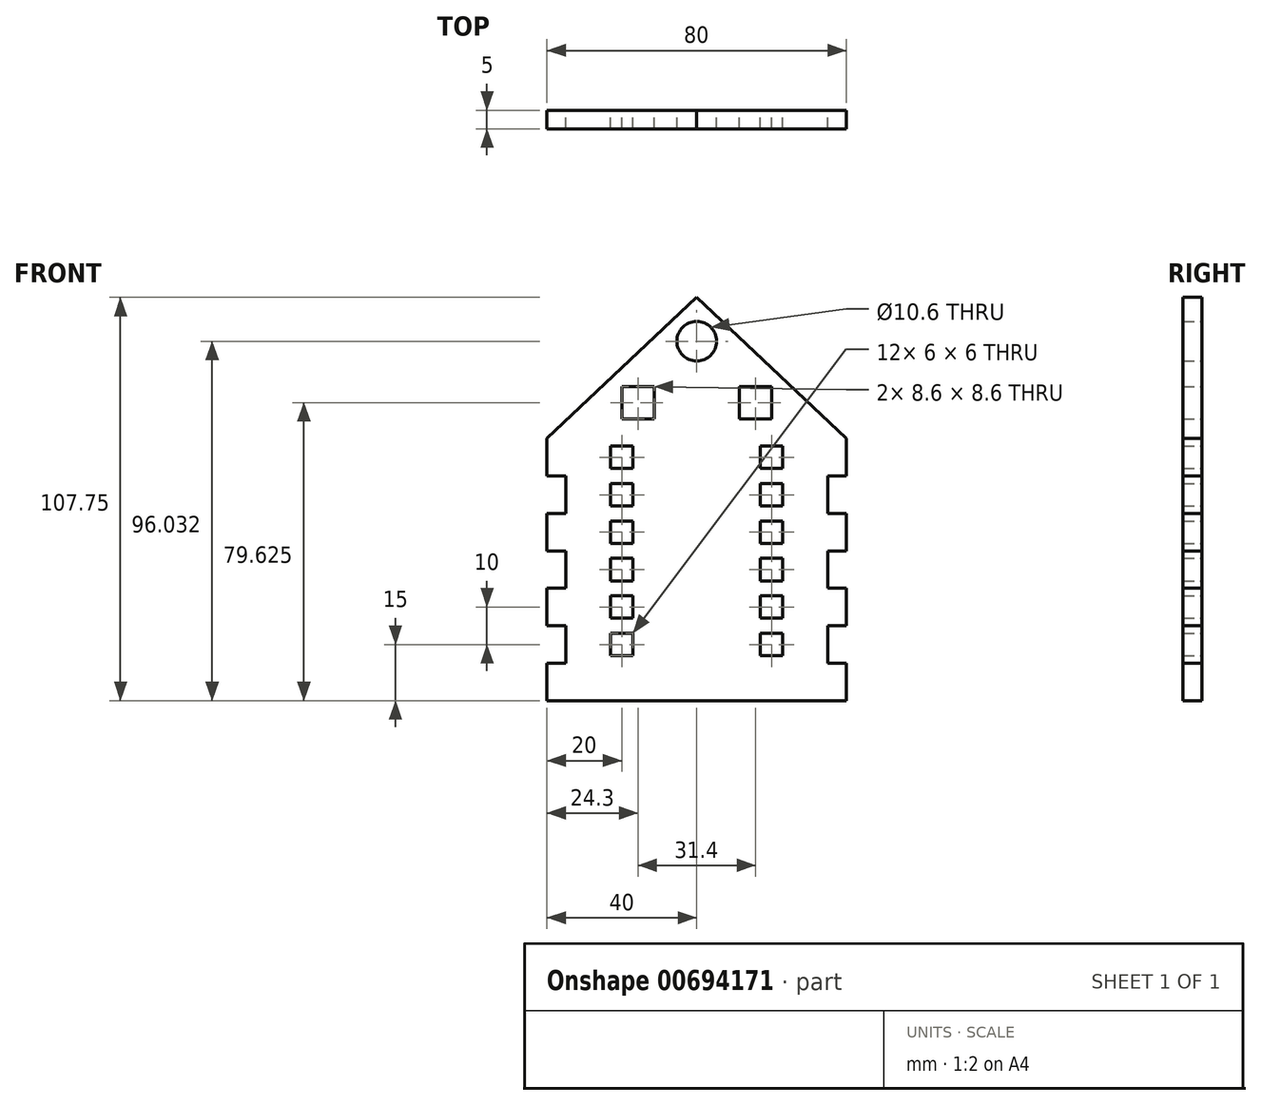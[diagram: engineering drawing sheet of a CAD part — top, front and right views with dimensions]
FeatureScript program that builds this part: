
annotation { "Feature Type Name" : "Feature", "Feature Type Description" : "" }
export const myFeature = defineFeature(function(context is Context, id is Id, definition is map)
    precondition{}
    {
        {
            var Q0;
            Q0=qCreatedBy(makeId("Front.planeOp"),FACE);
            var sketch = newSketch(context, id + "F0", { "sketchPlane" : qUnion([Q0])});
            skLineSegment(sketch, "E0.bottom", {"start": v(-40, 0) * mm, "end": v(0, 0) * mm});
            skLineSegment(sketch, "E0.top", {"start": v(-40, 70) * mm, "end": v(0, 70) * mm});
            skLineSegment(sketch, "E0.left", {"start": v(-40, 0) * mm, "end": v(-40, 10) * mm});
            skLineSegment(sketch, "E0.right", {"start": v(0, 0) * mm, "end": v(0, 70) * mm});
            skLineSegment(sketch, "E1", {"start": v(-14.13, 94.42) * mm, "end": v(-40, 70) * mm});
            skPoint(sketch, "E2.start.orphan", {"position": v(-20, 70) * mm});
            skLineSegment(sketch, "E3.bottom", {"start": v(-40, 60) * mm, "end": v(-35, 60) * mm});
            skLineSegment(sketch, "E3.top", {"start": v(-40, 50) * mm, "end": v(-35, 50) * mm});
            skLineSegment(sketch, "E3.right", {"start": v(-35, 60) * mm, "end": v(-35, 50) * mm});
            skLineSegment(sketch, "E4.bottom", {"start": v(-40, 20) * mm, "end": v(-35, 20) * mm});
            skLineSegment(sketch, "E4.top", {"start": v(-40, 10) * mm, "end": v(-35, 10) * mm});
            skLineSegment(sketch, "E4.right", {"start": v(-35, 20) * mm, "end": v(-35, 10) * mm});
            skLineSegment(sketch, "E5.bottom", {"start": v(-35, 40) * mm, "end": v(-40, 40) * mm});
            skLineSegment(sketch, "E5.top", {"start": v(-35, 30) * mm, "end": v(-40, 30) * mm});
            skLineSegment(sketch, "E5.left", {"start": v(-35, 40) * mm, "end": v(-35, 30) * mm});
            skLineSegment(sketch, "E6.trimOffspring", {"start": v(-40, 60) * mm, "end": v(-40, 70) * mm});
            skLineSegment(sketch, "E7.trimOffspring", {"start": v(-40, 40) * mm, "end": v(-40, 50) * mm});
            skLineSegment(sketch, "E8.trimOffspring", {"start": v(-40, 20) * mm, "end": v(-40, 30) * mm});
            skLineSegment(sketch, "E9.MirrorCS", {"start": v(40, 10) * mm, "end": v(35, 10) * mm});
            skLineSegment(sketch, "E10.MirrorCS", {"start": v(35, 30) * mm, "end": v(40, 30) * mm});
            skLineSegment(sketch, "E11.MirrorCS", {"start": v(35, 60) * mm, "end": v(35, 50) * mm});
            skLineSegment(sketch, "E12.MirrorCS", {"start": v(40, 60) * mm, "end": v(40, 70) * mm});
            skLineSegment(sketch, "E13.MirrorCS", {"start": v(40, 50) * mm, "end": v(35, 50) * mm});
            skLineSegment(sketch, "E14.MirrorCS", {"start": v(40, 60) * mm, "end": v(35, 60) * mm});
            skLineSegment(sketch, "E15.MirrorCS", {"start": v(40, 0) * mm, "end": v(40, 10) * mm});
            skLineSegment(sketch, "E16.MirrorCS", {"start": v(40, 40) * mm, "end": v(40, 50) * mm});
            skLineSegment(sketch, "E17.MirrorCS", {"start": v(40, 20) * mm, "end": v(35, 20) * mm});
            skLineSegment(sketch, "E18.MirrorCS", {"start": v(35, 20) * mm, "end": v(35, 10) * mm});
            skLineSegment(sketch, "E19.MirrorCS", {"start": v(40, 20) * mm, "end": v(40, 30) * mm});
            skLineSegment(sketch, "E20.MirrorCS", {"start": v(35, 40) * mm, "end": v(40, 40) * mm});
            skLineSegment(sketch, "E21.MirrorCS", {"start": v(35, 40) * mm, "end": v(35, 30) * mm});
            skLineSegment(sketch, "E22.MirrorCS", {"start": v(40, 70) * mm, "end": v(0, 70) * mm});
            skLineSegment(sketch, "E23.MirrorCS", {"start": v(14.13, 94.42) * mm, "end": v(40, 70) * mm});
            skLineSegment(sketch, "E24.MirrorCS", {"start": v(40, 0) * mm, "end": v(0, 0) * mm});
            skLineSegment(sketch, "E25", {"start": v(-14.13, 94.42) * mm, "end": v(0, 107.75) * mm});
            skLineSegment(sketch, "E26", {"start": v(14.13, 94.42) * mm, "end": v(0, 107.75) * mm});
            skLineSegment(sketch, "E27.bottom", {"start": v(-20, 83.92) * mm, "end": v(-11.4, 83.92) * mm});
            skLineSegment(sketch, "E27.top", {"start": v(-20, 75.32) * mm, "end": v(-11.4, 75.32) * mm});
            skLineSegment(sketch, "E27.left", {"start": v(-20, 83.92) * mm, "end": v(-20, 75.32) * mm});
            skLineSegment(sketch, "E27.right", {"start": v(-11.4, 83.92) * mm, "end": v(-11.4, 75.32) * mm});
            skLineSegment(sketch, "E28.bottom", {"start": v(20, 75.32) * mm, "end": v(11.4, 75.32) * mm});
            skLineSegment(sketch, "E28.top", {"start": v(20, 83.92) * mm, "end": v(11.4, 83.92) * mm});
            skLineSegment(sketch, "E28.left", {"start": v(20, 75.32) * mm, "end": v(20, 83.92) * mm});
            skLineSegment(sketch, "E28.right", {"start": v(11.4, 75.32) * mm, "end": v(11.4, 83.92) * mm});
            skCircle(sketch, "E29", {"center": v(0, 96.03) * mm, "radius": 5.3 * mm});
            skLineSegment(sketch, "E30", {"start": v(0, 101.33) * mm, "end": v(0, 90.73) * mm});
            skLineSegment(sketch, "E31", {"start": v(-5.3, 96.03) * mm, "end": v(5.3, 96.03) * mm});
            skLineSegment(sketch, "E32.bottom", {"start": v(-1.5, 0) * mm, "end": v(0, 0) * mm});
            skLineSegment(sketch, "E32.top", {"start": v(-1.5, 5.87) * mm, "end": v(0, 5.87) * mm});
            skLineSegment(sketch, "E32.left", {"start": v(-1.5, 0) * mm, "end": v(-1.5, 5.87) * mm});
            skLineSegment(sketch, "E32.right", {"start": v(0, 0) * mm, "end": v(0, 5.87) * mm});
            skLineSegment(sketch, "E33.MirrorCS", {"start": v(1.5, 0) * mm, "end": v(1.5, 5.87) * mm});
            skLineSegment(sketch, "E34.MirrorCS", {"start": v(1.5, 5.87) * mm, "end": v(0, 5.87) * mm});
            skLineSegment(sketch, "E35.bottom", {"start": v(-23, 18) * mm, "end": v(-17, 18) * mm});
            skLineSegment(sketch, "E35.top", {"start": v(-23, 12) * mm, "end": v(-17, 12) * mm});
            skLineSegment(sketch, "E35.left", {"start": v(-23, 18) * mm, "end": v(-23, 12) * mm});
            skLineSegment(sketch, "E35.right", {"start": v(-17, 18) * mm, "end": v(-17, 12) * mm});
            skLineSegment(sketch, "E36.bottom", {"start": v(-23, 28) * mm, "end": v(-17, 28) * mm});
            skLineSegment(sketch, "E36.top", {"start": v(-23, 22) * mm, "end": v(-17, 22) * mm});
            skLineSegment(sketch, "E36.left", {"start": v(-23, 28) * mm, "end": v(-23, 22) * mm});
            skLineSegment(sketch, "E36.right", {"start": v(-17, 28) * mm, "end": v(-17, 22) * mm});
            skLineSegment(sketch, "E37.bottom", {"start": v(-23, 38) * mm, "end": v(-17, 38) * mm});
            skLineSegment(sketch, "E37.top", {"start": v(-23, 32) * mm, "end": v(-17, 32) * mm});
            skLineSegment(sketch, "E37.left", {"start": v(-23, 38) * mm, "end": v(-23, 32) * mm});
            skLineSegment(sketch, "E37.right", {"start": v(-17, 38) * mm, "end": v(-17, 32) * mm});
            skLineSegment(sketch, "E38.bottom", {"start": v(-23, 48) * mm, "end": v(-17, 48) * mm});
            skLineSegment(sketch, "E38.top", {"start": v(-23, 42) * mm, "end": v(-17, 42) * mm});
            skLineSegment(sketch, "E38.left", {"start": v(-23, 48) * mm, "end": v(-23, 42) * mm});
            skLineSegment(sketch, "E38.right", {"start": v(-17, 48) * mm, "end": v(-17, 42) * mm});
            skLineSegment(sketch, "E39.bottom", {"start": v(-23, 58) * mm, "end": v(-17, 58) * mm});
            skLineSegment(sketch, "E39.top", {"start": v(-23, 52) * mm, "end": v(-17, 52) * mm});
            skLineSegment(sketch, "E39.left", {"start": v(-23, 58) * mm, "end": v(-23, 52) * mm});
            skLineSegment(sketch, "E39.right", {"start": v(-17, 58) * mm, "end": v(-17, 52) * mm});
            skLineSegment(sketch, "E40.bottom", {"start": v(-23, 68) * mm, "end": v(-17, 68) * mm});
            skLineSegment(sketch, "E40.top", {"start": v(-23, 62) * mm, "end": v(-17, 62) * mm});
            skLineSegment(sketch, "E40.left", {"start": v(-23, 68) * mm, "end": v(-23, 62) * mm});
            skLineSegment(sketch, "E40.right", {"start": v(-17, 68) * mm, "end": v(-17, 62) * mm});
            skLineSegment(sketch, "E41.MirrorCS", {"start": v(23, 28) * mm, "end": v(23, 22) * mm});
            skLineSegment(sketch, "E42.MirrorCS", {"start": v(23, 68) * mm, "end": v(23, 62) * mm});
            skLineSegment(sketch, "E43.MirrorCS", {"start": v(23, 32) * mm, "end": v(17, 32) * mm});
            skLineSegment(sketch, "E44.MirrorCS", {"start": v(23, 38) * mm, "end": v(17, 38) * mm});
            skLineSegment(sketch, "E45.MirrorCS", {"start": v(23, 22) * mm, "end": v(17, 22) * mm});
            skLineSegment(sketch, "E46.MirrorCS", {"start": v(23, 68) * mm, "end": v(17, 68) * mm});
            skLineSegment(sketch, "E47.MirrorCS", {"start": v(23, 18) * mm, "end": v(17, 18) * mm});
            skLineSegment(sketch, "E48.MirrorCS", {"start": v(17, 58) * mm, "end": v(17, 52) * mm});
            skLineSegment(sketch, "E49.MirrorCS", {"start": v(17, 38) * mm, "end": v(17, 32) * mm});
            skLineSegment(sketch, "E50.MirrorCS", {"start": v(23, 48) * mm, "end": v(17, 48) * mm});
            skLineSegment(sketch, "E51.MirrorCS", {"start": v(23, 28) * mm, "end": v(17, 28) * mm});
            skPoint(sketch, "E52.MirrorP", {"position": v(20, 70) * mm});
            skLineSegment(sketch, "E53.MirrorCS", {"start": v(23, 42) * mm, "end": v(17, 42) * mm});
            skLineSegment(sketch, "E54.MirrorCS", {"start": v(23, 12) * mm, "end": v(17, 12) * mm});
            skLineSegment(sketch, "E55.MirrorCS", {"start": v(17, 28) * mm, "end": v(17, 22) * mm});
            skLineSegment(sketch, "E56.MirrorCS", {"start": v(23, 58) * mm, "end": v(17, 58) * mm});
            skLineSegment(sketch, "E57.MirrorCS", {"start": v(17, 48) * mm, "end": v(17, 42) * mm});
            skLineSegment(sketch, "E58.MirrorCS", {"start": v(23, 48) * mm, "end": v(23, 42) * mm});
            skLineSegment(sketch, "E59.MirrorCS", {"start": v(23, 38) * mm, "end": v(23, 32) * mm});
            skLineSegment(sketch, "E60.MirrorCS", {"start": v(23, 58) * mm, "end": v(23, 52) * mm});
            skLineSegment(sketch, "E61.MirrorCS", {"start": v(23, 62) * mm, "end": v(17, 62) * mm});
            skLineSegment(sketch, "E62.MirrorCS", {"start": v(17, 68) * mm, "end": v(17, 62) * mm});
            skLineSegment(sketch, "E63.MirrorCS", {"start": v(23, 52) * mm, "end": v(17, 52) * mm});
            skLineSegment(sketch, "E64.MirrorCS", {"start": v(17, 18) * mm, "end": v(17, 12) * mm});
            skLineSegment(sketch, "E65.MirrorCS", {"start": v(23, 18) * mm, "end": v(23, 12) * mm});
            skLineSegment(sketch, "E66", {"start": v(-1.5, 0) * mm, "end": v(1.5, 0) * mm});
            skSolve(sketch);
        }
        {
            var Q0;
            Q0=qSketchRegion(id+"F0",true);
            extrude(context, id + "F1", {"entities" : qUnion([Q0]), "depth" : 5 * mm, "offsetDistance" : 25 * mm});
        }
    });
